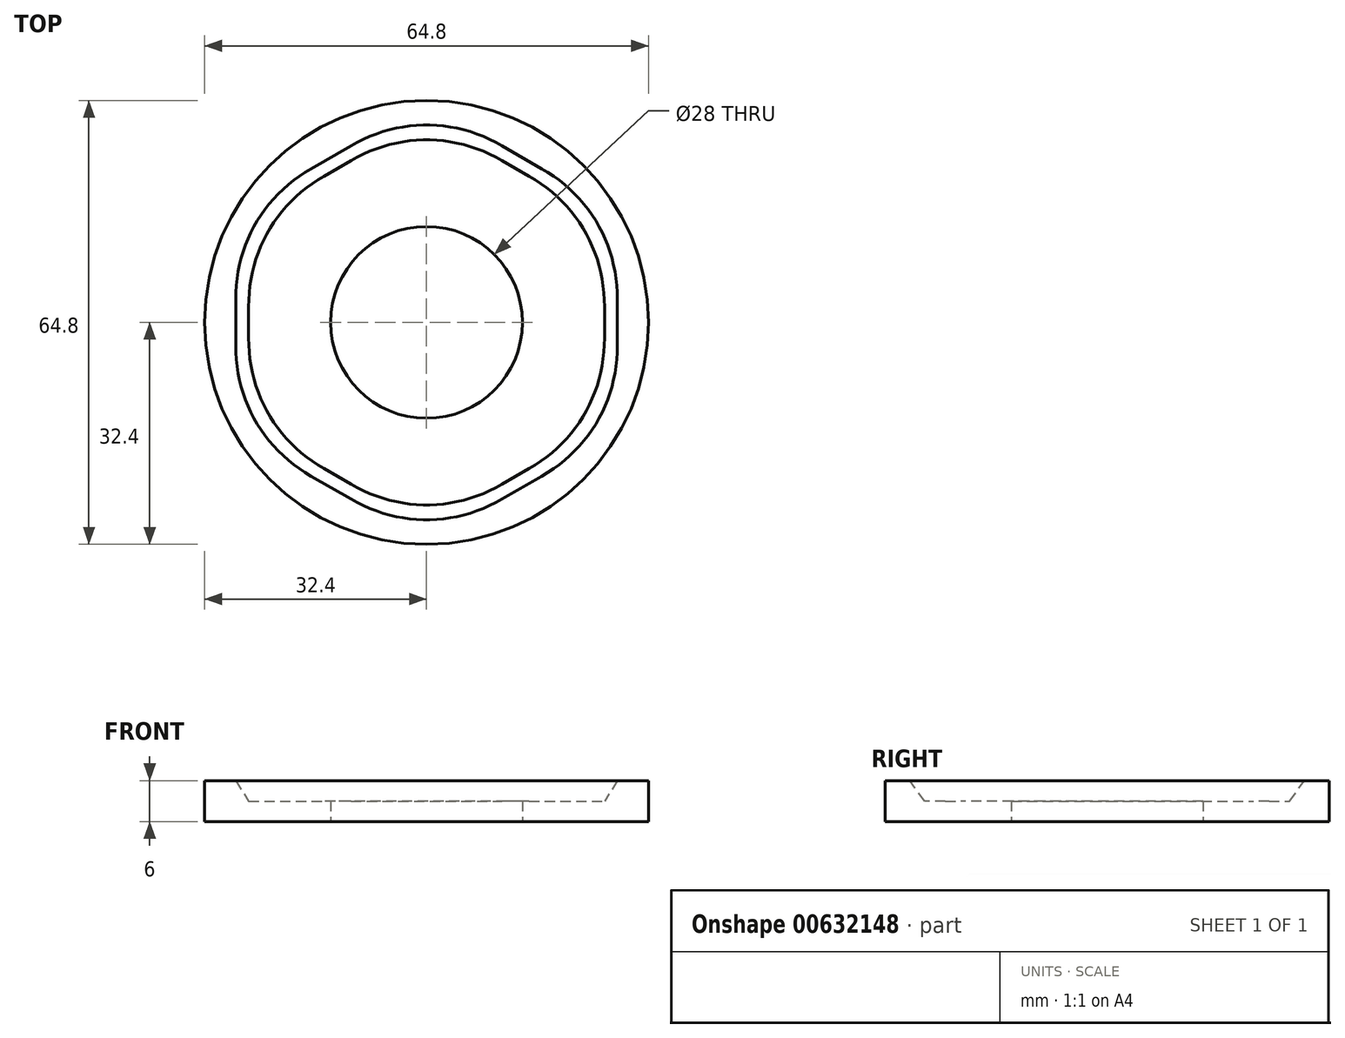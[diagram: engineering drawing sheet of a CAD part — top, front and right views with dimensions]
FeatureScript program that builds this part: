
annotation { "Feature Type Name" : "Feature", "Feature Type Description" : "" }
export const myFeature = defineFeature(function(context is Context, id is Id, definition is map)
    precondition{}
    {
        {
            var Q0;
            Q0=qCreatedBy(makeId("Top.planeOp"),FACE);
            var sketch = newSketch(context, id + "F0", { "sketchPlane" : qUnion([Q0])});
            skCircle(sketch, "E0", {"center": v(0, 0) * mm, "radius": 14 * mm});
            skCircle(sketch, "E1", {"center": v(0, 0) * mm, "radius": 30 * mm});
            skCircle(sketch, "E2.cCircle", {"center": v(0, 0) * mm, "radius": 30 * mm, "construction": true});
            skLineSegment(sketch, "E2.0", {"start": v(25.98, -15) * mm, "end": v(0, -30) * mm});
            skLineSegment(sketch, "E2.1", {"start": v(0, -30) * mm, "end": v(-25.98, -15) * mm});
            skLineSegment(sketch, "E2.2", {"start": v(-25.98, -15) * mm, "end": v(-25.98, 15) * mm});
            skLineSegment(sketch, "E2.3", {"start": v(-25.98, 15) * mm, "end": v(0, 30) * mm});
            skLineSegment(sketch, "E2.4", {"start": v(0, 30) * mm, "end": v(25.98, 15) * mm});
            skLineSegment(sketch, "E2.5", {"start": v(25.98, 15) * mm, "end": v(25.98, -15) * mm});
            skCircle(sketch, "E3.0", {"center": v(0, 0) * mm, "radius": 32.4 * mm});
            skSolve(sketch);
        }
        {
            var Q0;
            {var subQ0=sQuery(id+"F0.wireOp",EDGE,"E2.0");Q0=makeQuery(id+"F0.imprint","IMPRINT",FACE,{"disambiguationData":[TD([[makeQuery(id+"F0.imprint","IMPRINT",EDGE,{"derivedFrom":subQ0}),1.0]])]});}
            var Q1;
            {var subQ0=sQuery(id+"F0.wireOp",EDGE,"E2.5");Q1=makeQuery(id+"F0.imprint","IMPRINT",FACE,{"disambiguationData":[TD([[makeQuery(id+"F0.imprint","IMPRINT",EDGE,{"derivedFrom":subQ0}),1.0]])]});}
            var Q2;
            {var subQ0=sQuery(id+"F0.wireOp",EDGE,"E2.4");Q2=makeQuery(id+"F0.imprint","IMPRINT",FACE,{"disambiguationData":[TD([[makeQuery(id+"F0.imprint","IMPRINT",EDGE,{"derivedFrom":subQ0}),1.0]])]});}
            var Q3;
            {var subQ0=sQuery(id+"F0.wireOp",EDGE,"E2.3");Q3=makeQuery(id+"F0.imprint","IMPRINT",FACE,{"disambiguationData":[TD([[makeQuery(id+"F0.imprint","IMPRINT",EDGE,{"derivedFrom":subQ0}),1.0]])]});}
            var Q4;
            {var subQ0=sQuery(id+"F0.wireOp",EDGE,"E2.2");Q4=makeQuery(id+"F0.imprint","IMPRINT",FACE,{"disambiguationData":[TD([[makeQuery(id+"F0.imprint","IMPRINT",EDGE,{"derivedFrom":subQ0}),1.0]])]});}
            var Q5;
            {var subQ0=sQuery(id+"F0.wireOp",EDGE,"E2.1");Q5=makeQuery(id+"F0.imprint","IMPRINT",FACE,{"disambiguationData":[TD([[makeQuery(id+"F0.imprint","IMPRINT",EDGE,{"derivedFrom":subQ0}),1.0]])]});}
            var Q6;
            Q6=makeQuery(id+"F0.imprint","IMPRINT",FACE,{"disambiguationData":[TD([[makeQuery(id+"F0.imprint","IMPRINT",EDGE,{"derivedFrom":sQuery(id+"F0.wireOp",EDGE,"E3.0")}),1.0]])]});
            extrude(context, id + "F1", {"entities" : qUnion([Q0, Q1, Q2, Q3, Q4, Q5, Q6]), "depth" : 6 * mm, "offsetDistance" : 25 * mm});
        }
        {
            var Q0;
            Q0=makeQuery(id+"F0.imprint","IMPRINT",FACE,{"disambiguationData":[TD([[makeQuery(id+"F0.imprint","IMPRINT",EDGE,{"derivedFrom":sQuery(id+"F0.wireOp",EDGE,"E0")}),-1.0]])]});
            extrude(context, id + "F2", {"entities" : qUnion([Q0]), "operationType" : NewBodyOperationType.ADD, "depth" : 3 * mm, "offsetDistance" : 25 * mm});
        }
        {
            var Q0;
            Q0=makeQuery(id+"F2.opExtrude","CAP_FACE",FACE,{"disambiguationData":[OSD([sQuery(id+"F0.wireOp",EDGE,"E0"),sQuery(id+"F0.wireOp",EDGE,"E2.0"),sQuery(id+"F0.wireOp",EDGE,"E2.1"),sQuery(id+"F0.wireOp",EDGE,"E2.2"),sQuery(id+"F0.wireOp",EDGE,"E2.3"),sQuery(id+"F0.wireOp",EDGE,"E2.4"),sQuery(id+"F0.wireOp",EDGE,"E2.5")])],"isStart":false});
            extrude(context, id + "F3", {"entities" : qUnion([Q0]), "operationType" : NewBodyOperationType.REMOVE, "depth" : 25 * mm, "offsetDistance" : 25 * mm, "hasDraft" : true, "draftAngle" : 32 * degree});
        }
        {
            var Q0;
            Q0=makeQuery(id+"F3.boolean.opBoolean","COPY",EDGE,{"derivedFrom":makeQuery(id+"F3.opExtrude","SWEPT_EDGE",EDGE,{"disambiguationData":[OSD([sQuery(id+"F0.wireOp",EDGE,"E1"),sQuery(id+"F0.wireOp",EDGE,"E2.2"),sQuery(id+"F0.wireOp",EDGE,"E2.3")])]})});
            var Q1;
            Q1=makeQuery(id+"F3.boolean.opBoolean","COPY",EDGE,{"derivedFrom":makeQuery(id+"F3.opExtrude","SWEPT_EDGE",EDGE,{"disambiguationData":[OSD([sQuery(id+"F0.wireOp",EDGE,"E1"),sQuery(id+"F0.wireOp",EDGE,"E2.3"),sQuery(id+"F0.wireOp",EDGE,"E2.4")])]})});
            var Q2;
            Q2=makeQuery(id+"F3.boolean.opBoolean","COPY",EDGE,{"derivedFrom":makeQuery(id+"F3.opExtrude","SWEPT_EDGE",EDGE,{"disambiguationData":[OSD([sQuery(id+"F0.wireOp",EDGE,"E1"),sQuery(id+"F0.wireOp",EDGE,"E2.4"),sQuery(id+"F0.wireOp",EDGE,"E2.5")])]})});
            var Q3;
            Q3=makeQuery(id+"F3.boolean.opBoolean","COPY",EDGE,{"derivedFrom":makeQuery(id+"F3.opExtrude","SWEPT_EDGE",EDGE,{"disambiguationData":[OSD([sQuery(id+"F0.wireOp",EDGE,"E1"),sQuery(id+"F0.wireOp",EDGE,"E2.0"),sQuery(id+"F0.wireOp",EDGE,"E2.5")])]})});
            var Q4;
            Q4=makeQuery(id+"F3.boolean.opBoolean","COPY",EDGE,{"derivedFrom":makeQuery(id+"F3.opExtrude","SWEPT_EDGE",EDGE,{"disambiguationData":[OSD([sQuery(id+"F0.wireOp",EDGE,"E1"),sQuery(id+"F0.wireOp",EDGE,"E2.0"),sQuery(id+"F0.wireOp",EDGE,"E2.1")])]})});
            var Q5;
            Q5=makeQuery(id+"F3.boolean.opBoolean","COPY",EDGE,{"derivedFrom":makeQuery(id+"F3.opExtrude","SWEPT_EDGE",EDGE,{"disambiguationData":[OSD([sQuery(id+"F0.wireOp",EDGE,"E1"),sQuery(id+"F0.wireOp",EDGE,"E2.1"),sQuery(id+"F0.wireOp",EDGE,"E2.2")])]})});
            fillet(context, id + "F4", {"entities" : qUnion([Q0, Q1, Q2, Q3, Q4, Q5]), "radius" : 26 * mm, "tangentPropagation" : true, "allowEdgeOverflow" : false});
        }
    });
